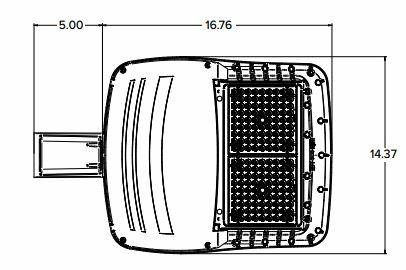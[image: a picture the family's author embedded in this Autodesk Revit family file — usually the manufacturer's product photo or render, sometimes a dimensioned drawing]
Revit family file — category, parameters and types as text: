
# Revit family: VP-1_A
name_source: partatom
category: Lighting Fixtures
units: mm (PartAtom-declared; Revit-internal decimal feet)

## family parameters
Cut with Voids When Loaded = No
Host = Face
Light Source = No
OmniClass Number = 23.80.70.11.14.17
OmniClass Title = Direct/Indirect
Part Type = Normal
Room Calculation Point = No
Round Connector Dimension = Use Diameter
Shared = Yes

## types (1)
- VP-1-A
    Apparent Load = 97 VA
    Assembly Code = D5020200
    Brand = Beacon
    CRI = 70
    Certification = UL
    Cool Grey = Cool Grey
    Default Elevation = 48 "
    Description = The Viper is an extremely versatile area/site luminaire which blends design, performance, and technology for a variety of applications.
    Features = Featuring two different optical technologies, Micro Strike and Strike Optics, which provide the best distribution patterns for retrofit or new construction
Vibration rated for high vibration applications including bridges and overpasses
Control options including photo control, occupancy sensing, NX Lighting Controls, wiSCAPE and 7-Pin with networked controls
Mounting options include: Arm, Universal Arm, Adjustable Arm, Mast Arm, Decorative Arm, Knuckle, Trunnion, Wall
Distribution options include: Auto Front Row, Type 2, Type 3, Type 4 Forward, Type 4 Wide, Type 5 Narrow, Type 5 Medium, Type 5 Wide, Type 5 Rectangular, Corner Optic, and Tennis Court
    Finish = Arctic White
    Glass = Glass
    Grey = Grey
    Lamp = LED
    Light Output = 6297 cd/m²
    Load Classification = Lighting
    Manufacturer = Current Lighting
    Matt Black = Matt Black
    Matt Grey = MATT GREY
    Matt White = Matt White
    Model = VP-1-A
    Name = Viper Area Size 1
    Power Factor = 0.9
    Product Documentation Link = https://cdn.currentlighting.com
    Product Page URL = https://www.currentlighting.com
    Type Comments = Lighting Fixture
    URL = https://www.currentlighting.com
    Voltage = 120 V
    Warranty = Five year warranty
    Wattage Comments = 97.2W

## geometry (parser evidence)
native form markers: Blend x2, Sweep x3
no freeform markers — native parametric forms only
